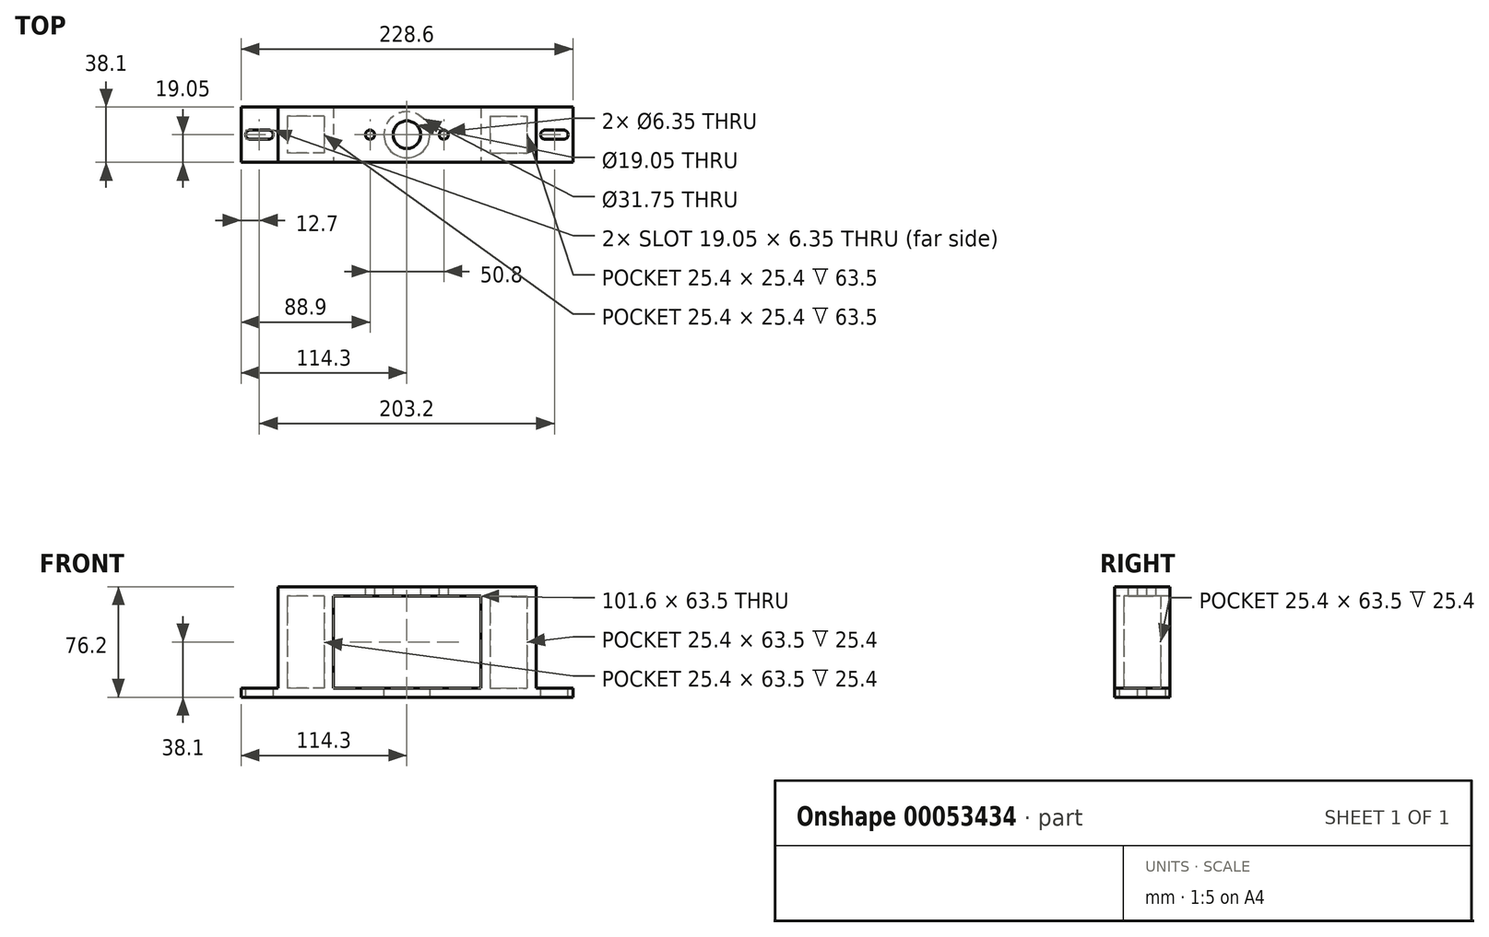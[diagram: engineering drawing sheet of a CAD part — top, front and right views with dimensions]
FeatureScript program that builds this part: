
annotation { "Feature Type Name" : "Feature", "Feature Type Description" : "" }
export const myFeature = defineFeature(function(context is Context, id is Id, definition is map)
    precondition{}
    {
        {
            var Q0;
            Q0=qCreatedBy(makeId("Top.planeOp"),FACE);
            var sketch = newSketch(context, id + "F0", { "sketchPlane" : qUnion([Q0])});
            skLineSegment(sketch, "E0.rect.bottom", {"start": v(114.3, 19.05) * mm, "end": v(-114.3, 19.05) * mm});
            skLineSegment(sketch, "E0.rect.top", {"start": v(114.3, -19.05) * mm, "end": v(-114.3, -19.05) * mm});
            skLineSegment(sketch, "E0.rect.left", {"start": v(114.3, 19.05) * mm, "end": v(114.3, -19.05) * mm});
            skLineSegment(sketch, "E0.rect.right", {"start": v(-114.3, 19.05) * mm, "end": v(-114.3, -19.05) * mm});
            skPoint(sketch, "E0.rect.middle", {"position": v(0, 0) * mm});
            skSolve(sketch);
        }
        {
            var Q0;
            Q0 = qSketchRegion(id + "F0", true);
            extrude(context, id + "F9", {"entities" : qUnion([Q0]), "depth" : 6.35 * mm});
        }
        {
            var Q0;
            Q0=makeQuery(id+"F9.opExtrude","CAP_FACE",FACE,{"disambiguationData":[OSD([sQuery(id+"F0.wireOp",EDGE,"E0.rect.bottom"),sQuery(id+"F0.wireOp",EDGE,"E0.rect.top"),sQuery(id+"F0.wireOp",EDGE,"E0.rect.left"),sQuery(id+"F0.wireOp",EDGE,"E0.rect.right")])],"isStart":false});
            var sketch = newSketch(context, id + "F1", { "sketchPlane" : qUnion([Q0])});
            skLineSegment(sketch, "E1.bottom", {"start": v(88.9, 19.05) * mm, "end": v(50.8, 19.05) * mm});
            skLineSegment(sketch, "E1.top", {"start": v(88.9, -19.05) * mm, "end": v(50.8, -19.05) * mm});
            skLineSegment(sketch, "E1.left", {"start": v(88.9, 19.05) * mm, "end": v(88.9, -19.05) * mm});
            skLineSegment(sketch, "E1.right", {"start": v(50.8, 19.05) * mm, "end": v(50.8, -19.05) * mm});
            skLineSegment(sketch, "E2.bottom", {"start": v(57.15, 12.7) * mm, "end": v(82.55, 12.7) * mm});
            skLineSegment(sketch, "E2.top", {"start": v(57.15, -12.7) * mm, "end": v(82.55, -12.7) * mm});
            skLineSegment(sketch, "E2.left", {"start": v(57.15, 12.7) * mm, "end": v(57.15, -12.7) * mm});
            skLineSegment(sketch, "E2.right", {"start": v(82.55, 12.7) * mm, "end": v(82.55, -12.7) * mm});
            skLineSegment(sketch, "E3.MirrorCS", {"start": v(-50.8, 19.05) * mm, "end": v(-50.8, -19.05) * mm});
            skLineSegment(sketch, "E4.MirrorCS", {"start": v(-57.15, 12.7) * mm, "end": v(-57.15, -12.7) * mm});
            skLineSegment(sketch, "E5.MirrorCS", {"start": v(-88.9, -19.05) * mm, "end": v(-50.8, -19.05) * mm});
            skLineSegment(sketch, "E6.MirrorCS", {"start": v(-57.15, -12.7) * mm, "end": v(-82.55, -12.7) * mm});
            skLineSegment(sketch, "E7.MirrorCS", {"start": v(-57.15, 12.7) * mm, "end": v(-82.55, 12.7) * mm});
            skLineSegment(sketch, "E8.MirrorCS", {"start": v(-88.9, 19.05) * mm, "end": v(-50.8, 19.05) * mm});
            skLineSegment(sketch, "E9.MirrorCS", {"start": v(-82.55, 12.7) * mm, "end": v(-82.55, -12.7) * mm});
            skLineSegment(sketch, "E10.MirrorCS", {"start": v(-88.9, 19.05) * mm, "end": v(-88.9, -19.05) * mm});
            skPoint(sketch, "E11.end.orphan", {"position": v(0, 19.05) * mm});
            skSolve(sketch);
        }
        {
            var Q0;
            Q0 = qSketchRegion(id + "F1", true);
            extrude(context, id + "F10", {"entities" : qUnion([Q0]), "operationType" : NewBodyOperationType.ADD, "depth" : 63.5 * mm});
        }
        {
            var Q0;
            Q0=makeQuery(id+"F10.opExtrude","CAP_FACE",FACE,{"disambiguationData":[OSD([sQuery(id+"F1.wireOp",EDGE,"E1.bottom"),sQuery(id+"F1.wireOp",EDGE,"E1.top"),sQuery(id+"F1.wireOp",EDGE,"E1.left"),sQuery(id+"F1.wireOp",EDGE,"E1.right"),sQuery(id+"F1.wireOp",EDGE,"E2.bottom"),sQuery(id+"F1.wireOp",EDGE,"E2.top"),sQuery(id+"F1.wireOp",EDGE,"E2.right"),sQuery(id+"F1.wireOp",EDGE,"E2.left")])],"isStart":false});
            var sketch = newSketch(context, id + "F11", { "sketchPlane" : qUnion([Q0])});
            skLineSegment(sketch, "E12.bottom", {"start": v(88.9, 19.05) * mm, "end": v(-88.9, 19.05) * mm});
            skLineSegment(sketch, "E12.top", {"start": v(88.9, -19.05) * mm, "end": v(-88.9, -19.05) * mm});
            skLineSegment(sketch, "E12.left", {"start": v(88.9, 19.05) * mm, "end": v(88.9, -19.05) * mm});
            skLineSegment(sketch, "E12.right", {"start": v(-88.9, 19.05) * mm, "end": v(-88.9, -19.05) * mm});
            skSolve(sketch);
        }
        {
            var Q0;
            Q0 = qSketchRegion(id + "F11", true);
            extrude(context, id + "F2", {"entities" : qUnion([Q0]), "operationType" : NewBodyOperationType.ADD, "depth" : 6.35 * mm});
        }
        {
            var Q0;
            Q0=makeQuery(id+"F2.opExtrude","CAP_FACE",FACE,{"disambiguationData":[OSD([sQuery(id+"F11.wireOp",EDGE,"E12.bottom"),sQuery(id+"F11.wireOp",EDGE,"E12.top"),sQuery(id+"F11.wireOp",EDGE,"E12.left"),sQuery(id+"F11.wireOp",EDGE,"E12.right")])],"isStart":false});
            var sketch = newSketch(context, id + "F3", { "sketchPlane" : qUnion([Q0])});
            skCircle(sketch, "E13", {"center": v(0, 0) * mm, "radius": 9.53 * mm});
            skCircle(sketch, "E14", {"center": v(25.4, 0) * mm, "radius": 3.18 * mm});
            skCircle(sketch, "E15", {"center": v(-25.4, 0) * mm, "radius": 3.18 * mm});
            skSolve(sketch);
        }
        {
            var Q0;
            Q0 = qSketchRegion(id + "F3", true);
            extrude(context, id + "F4", {"entities" : qUnion([Q0]), "operationType" : NewBodyOperationType.REMOVE, "oppositeDirection" : true, "depth" : 25.4 * mm});
        }
        {
            var Q0;
            {var subQ0=sQuery(id+"F0.wireOp",EDGE,"E0.rect.right");var subQ1=sQuery(id+"F0.wireOp",EDGE,"E0.rect.top");var subQ2=sQuery(id+"F0.wireOp",EDGE,"E0.rect.bottom");Q0=makeQuery(id+"F10.boolean.opBoolean","SPLIT",FACE,{"disambiguationData":[TD([makeQuery(id+"F9.opExtrude","SWEPT_FACE",FACE,{"disambiguationData":[OSD([subQ0])]})])],"derivedFrom":makeQuery(id+"F9.opExtrude","CAP_FACE",FACE,{"disambiguationData":[OSD([subQ2,subQ1,sQuery(id+"F0.wireOp",EDGE,"E0.rect.left"),subQ0])],"isStart":false})});}
            var sketch = newSketch(context, id + "F5", { "sketchPlane" : qUnion([Q0])});
            skLineSegment(sketch, "E16", {"start": v(-107.95, 3.18) * mm, "end": v(-95.25, 3.18) * mm});
            skLineSegment(sketch, "E17", {"start": v(-107.95, -3.17) * mm, "end": v(-95.25, -3.17) * mm});
            skArc(sketch, "E18", {"start": v(-95.25, 3.18) * mm, "mid": v(-92.08, 0) * mm, "end": v(-95.25, -3.17) * mm});
            skArc(sketch, "E19", {"start": v(-107.95, 3.18) * mm, "mid": v(-111.13, 0) * mm, "end": v(-107.95, -3.17) * mm});
            skLineSegment(sketch, "E20", {"start": v(0, 0) * mm, "end": v(0, -15.88) * mm});
            skLineSegment(sketch, "E21.MirrorCS", {"start": v(107.95, -3.17) * mm, "end": v(95.25, -3.17) * mm});
            skLineSegment(sketch, "E22.MirrorCS", {"start": v(107.95, 3.18) * mm, "end": v(95.25, 3.18) * mm});
            skArc(sketch, "E23.MirrorCS", {"start": v(95.25, 3.18) * mm, "mid": v(92.08, 0) * mm, "end": v(95.25, -3.17) * mm});
            skArc(sketch, "E24.MirrorCS", {"start": v(107.95, 3.18) * mm, "mid": v(111.13, 0) * mm, "end": v(107.95, -3.17) * mm});
            skSolve(sketch);
        }
        {
            var Q0;
            Q0 = qSketchRegion(id + "F5", true);
            extrude(context, id + "F6", {"entities" : qUnion([Q0]), "operationType" : NewBodyOperationType.REMOVE, "endBound" : BoundingType.THROUGH_ALL, "oppositeDirection" : true, "depth" : 25.4 * mm});
        }
        {
            var Q0;
            Q0=makeQuery(id+"F9.opExtrude","CAP_FACE",FACE,{"disambiguationData":[OSD([sQuery(id+"F0.wireOp",EDGE,"E0.rect.bottom"),sQuery(id+"F0.wireOp",EDGE,"E0.rect.top"),sQuery(id+"F0.wireOp",EDGE,"E0.rect.left"),sQuery(id+"F0.wireOp",EDGE,"E0.rect.right")])],"isStart":true});
            var sketch = newSketch(context, id + "F7", { "sketchPlane" : qUnion([Q0])});
            skCircle(sketch, "E25", {"center": v(0, 0) * mm, "radius": 15.88 * mm});
            skSolve(sketch);
        }
        {
            var Q0;
            Q0=makeQuery(id+"F7.imprint","IMPRINT",FACE,{"disambiguationData":[TD([[makeQuery(id+"F7.imprint","IMPRINT",EDGE,{"derivedFrom":sQuery(id+"F7.wireOp",EDGE,"E25")}),1.0]])]});
            extrude(context, id + "F8", {"entities" : qUnion([Q0]), "operationType" : NewBodyOperationType.REMOVE, "oppositeDirection" : true, "depth" : 25.4 * mm});
        }
    });
